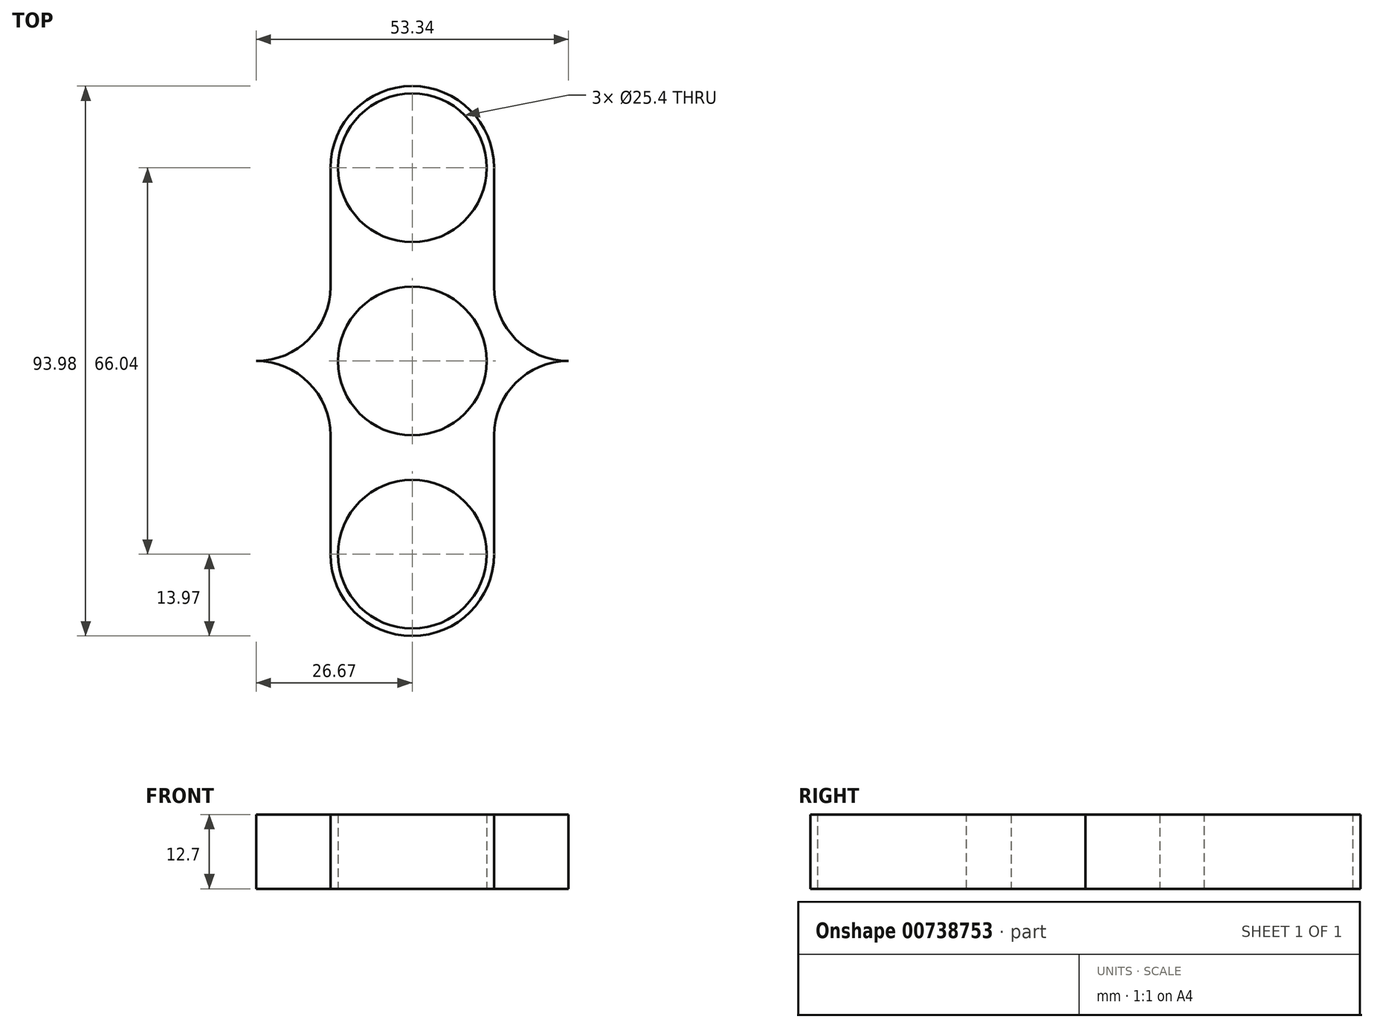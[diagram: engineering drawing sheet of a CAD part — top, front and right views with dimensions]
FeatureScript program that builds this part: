
annotation { "Feature Type Name" : "Feature", "Feature Type Description" : "" }
export const myFeature = defineFeature(function(context is Context, id is Id, definition is map)
    precondition{}
    {
        {
            var Q0;
            Q0=qCreatedBy(makeId("Top.planeOp"),FACE);
            var sketch = newSketch(context, id + "F0", { "sketchPlane" : qUnion([Q0])});
            skCircle(sketch, "E0", {"center": v(0, 33.02) * mm, "radius": 13.97 * mm});
            skCircle(sketch, "E1", {"center": v(0, -33.02) * mm, "radius": 13.97 * mm});
            skCircle(sketch, "E2", {"center": v(0, 0) * mm, "radius": 12.7 * mm});
            skLineSegment(sketch, "E3", {"start": v(-13.97, 33.02) * mm, "end": v(-13.97, -33.02) * mm});
            skLineSegment(sketch, "E4", {"start": v(13.97, 33.02) * mm, "end": v(13.97, -33.02) * mm});
            skArc(sketch, "E5", {"start": v(-13.97, -12.7) * mm, "mid": v(-17.69, -3.72) * mm, "end": v(-26.67, 0) * mm});
            skArc(sketch, "E6", {"start": v(-26.67, 0) * mm, "mid": v(-17.69, 3.72) * mm, "end": v(-13.97, 12.7) * mm});
            skLineSegment(sketch, "E7", {"start": v(0, 59.6) * mm, "end": v(0, -57.9) * mm, "construction": true});
            skArc(sketch, "E8.MirrorC", {"start": v(26.67, 0) * mm, "mid": v(17.69, 3.72) * mm, "end": v(13.97, 12.7) * mm});
            skArc(sketch, "E9.MirrorC", {"start": v(13.97, -12.7) * mm, "mid": v(17.69, -3.72) * mm, "end": v(26.67, 0) * mm});
            skSolve(sketch);
        }
        {
            var Q0;
            Q0 = qSketchRegion(id + "F0", true);
            extrude(context, id + "F1", {"entities" : qUnion([Q0]), "depth" : 12.7 * mm, "offsetDistance" : 25.4 * mm});
        }
        {
            var Q0;
            Q0=makeQuery(id+"F1.opExtrude","CAP_FACE",FACE,{"disambiguationData":[OSD([sQuery(id+"F0.wireOp",EDGE,"E0"),sQuery(id+"F0.wireOp",EDGE,"E1"),sQuery(id+"F0.wireOp",EDGE,"E2"),sQuery(id+"F0.wireOp",EDGE,"E3"),sQuery(id+"F0.wireOp",EDGE,"E4"),sQuery(id+"F0.wireOp",EDGE,"E5"),sQuery(id+"F0.wireOp",EDGE,"E6"),sQuery(id+"F0.wireOp",EDGE,"E8.MirrorC"),sQuery(id+"F0.wireOp",EDGE,"E9.MirrorC")])],"isStart":false});
            var sketch = newSketch(context, id + "F2", { "sketchPlane" : qUnion([Q0])});
            skCircle(sketch, "E10", {"center": v(0, 33.02) * mm, "radius": 12.7 * mm});
            skCircle(sketch, "E11", {"center": v(0, -33.02) * mm, "radius": 12.7 * mm});
            skSolve(sketch);
        }
        {
            var Q0;
            Q0 = qSketchRegion(id + "F2", true);
            extrude(context, id + "F3", {"entities" : qUnion([Q0]), "operationType" : NewBodyOperationType.REMOVE, "oppositeDirection" : true, "depth" : 25.4 * mm, "offsetDistance" : 25.4 * mm});
        }
    });
